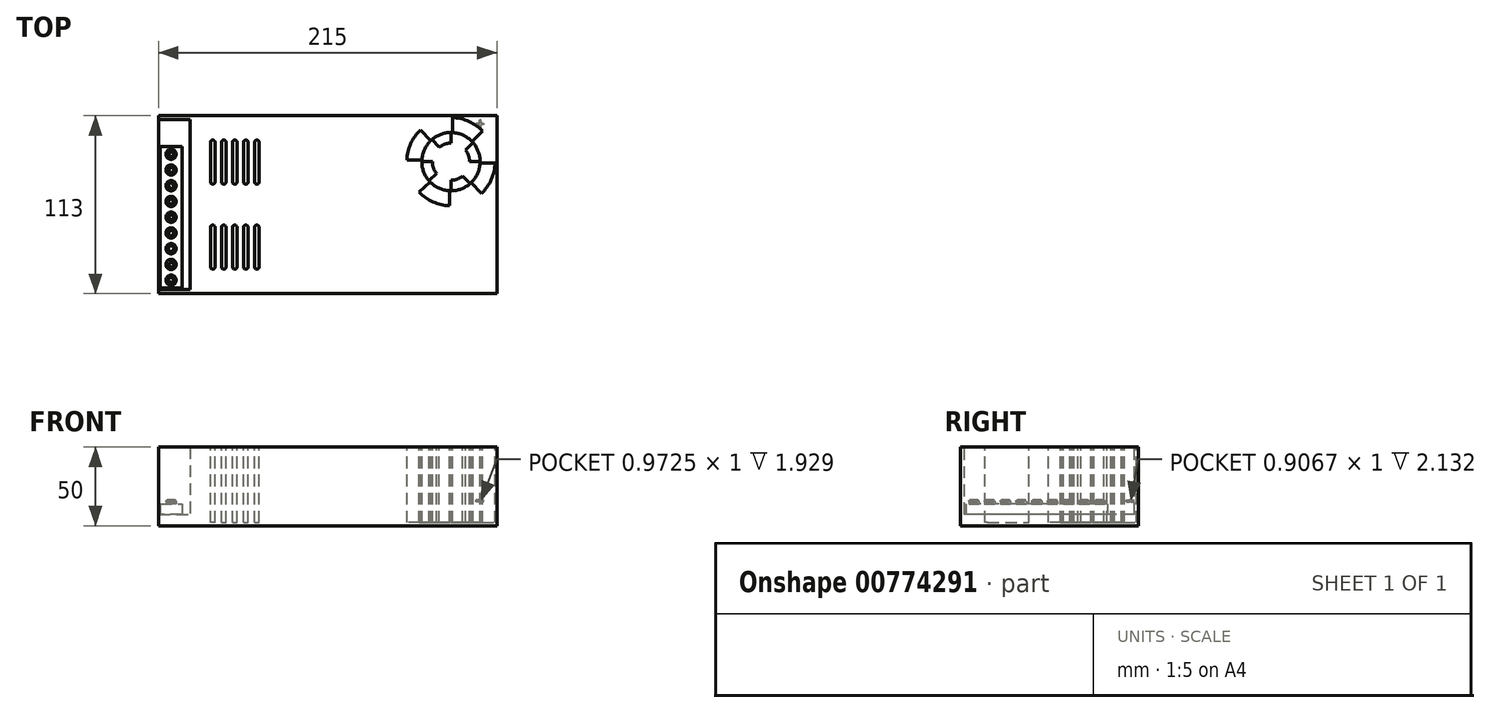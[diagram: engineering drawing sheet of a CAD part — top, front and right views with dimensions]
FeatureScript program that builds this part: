
annotation { "Feature Type Name" : "Feature", "Feature Type Description" : "" }
export const myFeature = defineFeature(function(context is Context, id is Id, definition is map)
    precondition{}
    {
        {
            var Q0;
            Q0=qCreatedBy(makeId("Top.planeOp"),FACE);
            var sketch = newSketch(context, id + "F0", { "sketchPlane" : qUnion([Q0])});
            skLineSegment(sketch, "E0.bottom", {"start": v(-204.25, 5.3) * mm, "end": v(10.75, 5.3) * mm});
            skLineSegment(sketch, "E0.top", {"start": v(-204.25, -107.7) * mm, "end": v(10.75, -107.7) * mm});
            skLineSegment(sketch, "E0.left", {"start": v(-204.25, 5.3) * mm, "end": v(-204.25, -107.7) * mm});
            skLineSegment(sketch, "E0.right", {"start": v(10.75, 5.3) * mm, "end": v(10.75, -107.7) * mm});
            skLineSegment(sketch, "E1", {"start": v(-184.25, 5.3) * mm, "end": v(-184.25, -107.7) * mm});
            skSolve(sketch);
        }
        {
            var Q0;
            {var subQ0=sQuery(id+"F0.wireOp",EDGE,"E0.left");Q0=makeQuery(id+"F0.imprint","IMPRINT",FACE,{"disambiguationData":[TD([[makeQuery(id+"F0.imprint","IMPRINT",EDGE,{"derivedFrom":subQ0}),1.0]])]});}
            extrude(context, id + "F1", {"entities" : qUnion([Q0]), "depth" : .8 * mm, "offsetDistance" : 25 * mm});
        }
        {
            var Q0;
            {var subQ0=sQuery(id+"F0.wireOp",EDGE,"E0.right");Q0=makeQuery(id+"F0.imprint","IMPRINT",FACE,{"disambiguationData":[TD([[makeQuery(id+"F0.imprint","IMPRINT",EDGE,{"derivedFrom":subQ0}),-1.0]])]});}
            extrude(context, id + "F2", {"entities" : qUnion([Q0]), "operationType" : NewBodyOperationType.ADD, "depth" : 50 * mm, "offsetDistance" : 25 * mm});
        }
        {
            var Q0;
            Q0=sQuery(id+"F0.wireOp",EDGE,"E0.bottom");
            extrude(context, id + "F3", {"bodyType" : ToolBodyType.SURFACE, "surfaceEntities" : qUnion([Q0]), "depth" : 50 * mm, "offsetDistance" : 25 * mm});
        }
        {
            var Q0;
            Q0=makeQuery(id+"F3.opExtrude","SWEPT_FACE",FACE,{"disambiguationData":[OSD([sQuery(id+"F0.wireOp",EDGE,"E0.bottom")])]});
            extrude(context, id + "F4", {"entities" : qUnion([Q0]), "operationType" : NewBodyOperationType.ADD, "depth" : 2.5 * mm, "offsetDistance" : 25 * mm});
        }
        {
            var Q0;
            Q0=sQuery(id+"F0.wireOp",EDGE,"E0.top");
            extrude(context, id + "F5", {"bodyType" : ToolBodyType.SURFACE, "surfaceEntities" : qUnion([Q0]), "depth" : 50 * mm, "offsetDistance" : 25 * mm});
        }
        {
            var Q0;
            Q0=makeQuery(id+"F5.opExtrude","SWEPT_FACE",FACE,{"disambiguationData":[OSD([sQuery(id+"F0.wireOp",EDGE,"E0.top")])]});
            extrude(context, id + "F6", {"entities" : qUnion([Q0]), "operationType" : NewBodyOperationType.ADD, "oppositeDirection" : true, "depth" : 2.5 * mm, "offsetDistance" : 25 * mm});
        }
        {
            var Q0;
            Q0=makeQuery(id+"F1.opExtrude","CAP_FACE",FACE,{"disambiguationData":[OSD([sQuery(id+"F0.wireOp",EDGE,"E0.bottom"),sQuery(id+"F0.wireOp",EDGE,"E0.top"),sQuery(id+"F0.wireOp",EDGE,"E0.left"),sQuery(id+"F0.wireOp",EDGE,"E1")])],"isStart":false});
            extrude(context, id + "F7", {"entities" : qUnion([Q0]), "operationType" : NewBodyOperationType.ADD, "depth" : 6.5 * mm, "offsetDistance" : 25 * mm});
        }
        {
            var Q0;
            Q0=makeQuery(id+"F7.opExtrude","CAP_FACE",FACE,{"disambiguationData":[OSD([sQuery(id+"F0.wireOp",EDGE,"E0.bottom"),sQuery(id+"F0.wireOp",EDGE,"E0.top"),sQuery(id+"F0.wireOp",EDGE,"E0.left"),sQuery(id+"F0.wireOp",EDGE,"E1")])],"isStart":false});
            var sketch = newSketch(context, id + "F8", { "sketchPlane" : qUnion([Q0])});
            skLineSegment(sketch, "E2.bottom", {"start": v(-203.25, -14.2) * mm, "end": v(-189.25, -14.2) * mm});
            skLineSegment(sketch, "E2.left", {"start": v(-203.25, -14.2) * mm, "end": v(-203.25, -101.2) * mm});
            skLineSegment(sketch, "E2.right", {"start": v(-189.25, -14.2) * mm, "end": v(-189.25, -104.2) * mm});
            skLineSegment(sketch, "E3", {"start": v(-189.25, -24.2) * mm, "end": v(-203.25, -24.2) * mm});
            skLineSegment(sketch, "E4", {"start": v(-189.25, -34.2) * mm, "end": v(-203.25, -34.2) * mm});
            skLineSegment(sketch, "E5", {"start": v(-189.25, -44.2) * mm, "end": v(-203.25, -44.2) * mm});
            skLineSegment(sketch, "E6", {"start": v(-189.25, -54.2) * mm, "end": v(-203.25, -54.2) * mm});
            skLineSegment(sketch, "E7", {"start": v(-189.25, -64.2) * mm, "end": v(-203.25, -64.2) * mm});
            skLineSegment(sketch, "E8", {"start": v(-189.25, -74.2) * mm, "end": v(-203.25, -74.2) * mm});
            skLineSegment(sketch, "E9", {"start": v(-189.25, -84.2) * mm, "end": v(-203.25, -84.2) * mm});
            skLineSegment(sketch, "E10", {"start": v(-189.25, -94.2) * mm, "end": v(-203.25, -94.2) * mm});
            skLineSegment(sketch, "E11", {"start": v(-189.25, -104.2) * mm, "end": v(-203.25, -104.2) * mm});
            skLineSegment(sketch, "E12", {"start": v(-203.25, -101.2) * mm, "end": v(-203.25, -104.2) * mm});
            skLineSegment(sketch, "E13", {"start": v(-196.25, -14.2) * mm, "end": v(-196.25, -24.2) * mm});
            skCircle(sketch, "E14", {"center": v(-196.25, -19.2) * mm, "radius": 3.25 * mm});
            skLineSegment(sketch, "E15", {"start": v(-189.25, -24.2) * mm, "end": v(-203.25, -34.2) * mm});
            skLineSegment(sketch, "E16", {"start": v(-189.25, -34.2) * mm, "end": v(-203.25, -44.2) * mm});
            skLineSegment(sketch, "E17", {"start": v(-189.25, -44.2) * mm, "end": v(-203.25, -54.2) * mm});
            skLineSegment(sketch, "E18", {"start": v(-189.25, -54.2) * mm, "end": v(-203.25, -64.2) * mm});
            skLineSegment(sketch, "E19", {"start": v(-189.25, -64.2) * mm, "end": v(-203.25, -74.2) * mm});
            skLineSegment(sketch, "E20", {"start": v(-189.25, -74.2) * mm, "end": v(-203.25, -84.2) * mm});
            skLineSegment(sketch, "E21", {"start": v(-189.25, -84.2) * mm, "end": v(-203.25, -94.2) * mm});
            skLineSegment(sketch, "E22", {"start": v(-189.25, -94.2) * mm, "end": v(-203.25, -104.2) * mm});
            skCircle(sketch, "E23", {"center": v(-196.25, -29.2) * mm, "radius": 3.25 * mm});
            skCircle(sketch, "E24", {"center": v(-196.25, -39.2) * mm, "radius": 3.25 * mm});
            skCircle(sketch, "E25", {"center": v(-196.25, -49.2) * mm, "radius": 3.25 * mm});
            skCircle(sketch, "E26", {"center": v(-196.25, -59.2) * mm, "radius": 3.25 * mm});
            skCircle(sketch, "E27", {"center": v(-196.25, -69.2) * mm, "radius": 3.25 * mm});
            skCircle(sketch, "E28", {"center": v(-196.25, -79.2) * mm, "radius": 3.25 * mm});
            skCircle(sketch, "E29", {"center": v(-196.25, -89.2) * mm, "radius": 3.25 * mm});
            skCircle(sketch, "E30", {"center": v(-196.25, -99.2) * mm, "radius": 3.25 * mm});
            skSolve(sketch);
        }
        {
            var Q0;
            Q0 = qSketchRegion(id + "F8", true);
            extrude(context, id + "F9", {"entities" : qUnion([Q0]), "operationType" : NewBodyOperationType.ADD, "depth" : 6.5 * mm, "offsetDistance" : 25 * mm});
        }
        {
            var Q0;
            Q0=makeQuery(id+"F9.boolean.opBoolean","SPLIT",FACE,{"disambiguationData":[TD([makeQuery(id+"F9.opExtrude","SWEPT_FACE",FACE,{"disambiguationData":[OSD([sQuery(id+"F8.wireOp",EDGE,"E14")])]})])],"derivedFrom":makeQuery(id+"F7.opExtrude","CAP_FACE",FACE,{"disambiguationData":[OSD([sQuery(id+"F0.wireOp",EDGE,"E0.bottom"),sQuery(id+"F0.wireOp",EDGE,"E0.top"),sQuery(id+"F0.wireOp",EDGE,"E0.left"),sQuery(id+"F0.wireOp",EDGE,"E1")])],"isStart":false})});
            var Q1;
            Q1=makeQuery(id+"F9.boolean.opBoolean","SPLIT",FACE,{"disambiguationData":[TD([makeQuery(id+"F9.opExtrude","SWEPT_FACE",FACE,{"disambiguationData":[OSD([sQuery(id+"F8.wireOp",EDGE,"E23")])]})])],"derivedFrom":makeQuery(id+"F7.opExtrude","CAP_FACE",FACE,{"disambiguationData":[OSD([sQuery(id+"F0.wireOp",EDGE,"E0.bottom"),sQuery(id+"F0.wireOp",EDGE,"E0.top"),sQuery(id+"F0.wireOp",EDGE,"E0.left"),sQuery(id+"F0.wireOp",EDGE,"E1")])],"isStart":false})});
            var Q2;
            Q2=makeQuery(id+"F9.boolean.opBoolean","SPLIT",FACE,{"disambiguationData":[TD([makeQuery(id+"F9.opExtrude","SWEPT_FACE",FACE,{"disambiguationData":[OSD([sQuery(id+"F8.wireOp",EDGE,"E24")])]})])],"derivedFrom":makeQuery(id+"F7.opExtrude","CAP_FACE",FACE,{"disambiguationData":[OSD([sQuery(id+"F0.wireOp",EDGE,"E0.bottom"),sQuery(id+"F0.wireOp",EDGE,"E0.top"),sQuery(id+"F0.wireOp",EDGE,"E0.left"),sQuery(id+"F0.wireOp",EDGE,"E1")])],"isStart":false})});
            var Q3;
            Q3=makeQuery(id+"F9.boolean.opBoolean","SPLIT",FACE,{"disambiguationData":[TD([makeQuery(id+"F9.opExtrude","SWEPT_FACE",FACE,{"disambiguationData":[OSD([sQuery(id+"F8.wireOp",EDGE,"E25")])]})])],"derivedFrom":makeQuery(id+"F7.opExtrude","CAP_FACE",FACE,{"disambiguationData":[OSD([sQuery(id+"F0.wireOp",EDGE,"E0.bottom"),sQuery(id+"F0.wireOp",EDGE,"E0.top"),sQuery(id+"F0.wireOp",EDGE,"E0.left"),sQuery(id+"F0.wireOp",EDGE,"E1")])],"isStart":false})});
            var Q4;
            Q4=makeQuery(id+"F9.boolean.opBoolean","SPLIT",FACE,{"disambiguationData":[TD([makeQuery(id+"F9.opExtrude","SWEPT_FACE",FACE,{"disambiguationData":[OSD([sQuery(id+"F8.wireOp",EDGE,"E26")])]})])],"derivedFrom":makeQuery(id+"F7.opExtrude","CAP_FACE",FACE,{"disambiguationData":[OSD([sQuery(id+"F0.wireOp",EDGE,"E0.bottom"),sQuery(id+"F0.wireOp",EDGE,"E0.top"),sQuery(id+"F0.wireOp",EDGE,"E0.left"),sQuery(id+"F0.wireOp",EDGE,"E1")])],"isStart":false})});
            var Q5;
            Q5=makeQuery(id+"F9.boolean.opBoolean","SPLIT",FACE,{"disambiguationData":[TD([makeQuery(id+"F9.opExtrude","SWEPT_FACE",FACE,{"disambiguationData":[OSD([sQuery(id+"F8.wireOp",EDGE,"E27")])]})])],"derivedFrom":makeQuery(id+"F7.opExtrude","CAP_FACE",FACE,{"disambiguationData":[OSD([sQuery(id+"F0.wireOp",EDGE,"E0.bottom"),sQuery(id+"F0.wireOp",EDGE,"E0.top"),sQuery(id+"F0.wireOp",EDGE,"E0.left"),sQuery(id+"F0.wireOp",EDGE,"E1")])],"isStart":false})});
            var Q6;
            Q6=makeQuery(id+"F9.boolean.opBoolean","SPLIT",FACE,{"disambiguationData":[TD([makeQuery(id+"F9.opExtrude","SWEPT_FACE",FACE,{"disambiguationData":[OSD([sQuery(id+"F8.wireOp",EDGE,"E28")])]})])],"derivedFrom":makeQuery(id+"F7.opExtrude","CAP_FACE",FACE,{"disambiguationData":[OSD([sQuery(id+"F0.wireOp",EDGE,"E0.bottom"),sQuery(id+"F0.wireOp",EDGE,"E0.top"),sQuery(id+"F0.wireOp",EDGE,"E0.left"),sQuery(id+"F0.wireOp",EDGE,"E1")])],"isStart":false})});
            var Q7;
            Q7=makeQuery(id+"F9.boolean.opBoolean","SPLIT",FACE,{"disambiguationData":[TD([makeQuery(id+"F9.opExtrude","SWEPT_FACE",FACE,{"disambiguationData":[OSD([sQuery(id+"F8.wireOp",EDGE,"E29")])]})])],"derivedFrom":makeQuery(id+"F7.opExtrude","CAP_FACE",FACE,{"disambiguationData":[OSD([sQuery(id+"F0.wireOp",EDGE,"E0.bottom"),sQuery(id+"F0.wireOp",EDGE,"E0.top"),sQuery(id+"F0.wireOp",EDGE,"E0.left"),sQuery(id+"F0.wireOp",EDGE,"E1")])],"isStart":false})});
            var Q8;
            Q8=makeQuery(id+"F9.boolean.opBoolean","SPLIT",FACE,{"disambiguationData":[TD([makeQuery(id+"F9.opExtrude","SWEPT_FACE",FACE,{"disambiguationData":[OSD([sQuery(id+"F8.wireOp",EDGE,"E30")])]})])],"derivedFrom":makeQuery(id+"F7.opExtrude","CAP_FACE",FACE,{"disambiguationData":[OSD([sQuery(id+"F0.wireOp",EDGE,"E0.bottom"),sQuery(id+"F0.wireOp",EDGE,"E0.top"),sQuery(id+"F0.wireOp",EDGE,"E0.left"),sQuery(id+"F0.wireOp",EDGE,"E1")])],"isStart":false})});
            var Q9;
            Q9=sQuery(id+"F8.wireOp",EDGE,"E23");
            var Q10;
            Q10=sQuery(id+"F8.wireOp",EDGE,"E14");
            var Q11;
            Q11=sQuery(id+"F8.wireOp",EDGE,"E24");
            var Q12;
            Q12=sQuery(id+"F8.wireOp",EDGE,"E25");
            var Q13;
            Q13=sQuery(id+"F8.wireOp",EDGE,"E26");
            var Q14;
            Q14=sQuery(id+"F8.wireOp",EDGE,"E27");
            var Q15;
            Q15=sQuery(id+"F8.wireOp",EDGE,"E28");
            var Q16;
            Q16=sQuery(id+"F8.wireOp",EDGE,"E29");
            var Q17;
            Q17=sQuery(id+"F8.wireOp",EDGE,"E30");
            extrude(context, id + "F10", {"entities" : qUnion([Q0, Q1, Q2, Q3, Q4, Q5, Q6, Q7, Q8]), "operationType" : NewBodyOperationType.ADD, "surfaceOperationType" : NewSurfaceOperationType.ADD, "surfaceEntities" : qUnion([Q9, Q10, Q11, Q12, Q13, Q14, Q15, Q16, Q17]), "depth" : 9 * mm, "offsetDistance" : 25 * mm});
        }
        {
            var Q0;
            Q0=makeQuery(id+"F10.opExtrude","CAP_EDGE",EDGE,{"disambiguationData":[OSD([sQuery(id+"F8.wireOp",EDGE,"E14")])],"isStart":false});
            var Q1;
            Q1=makeQuery(id+"F10.opExtrude","CAP_EDGE",EDGE,{"disambiguationData":[OSD([sQuery(id+"F8.wireOp",EDGE,"E23")])],"isStart":false});
            var Q2;
            Q2=makeQuery(id+"F10.opExtrude","CAP_EDGE",EDGE,{"disambiguationData":[OSD([sQuery(id+"F8.wireOp",EDGE,"E24")])],"isStart":false});
            var Q3;
            Q3=makeQuery(id+"F10.opExtrude","CAP_EDGE",EDGE,{"disambiguationData":[OSD([sQuery(id+"F8.wireOp",EDGE,"E25")])],"isStart":false});
            var Q4;
            Q4=makeQuery(id+"F10.opExtrude","CAP_EDGE",EDGE,{"disambiguationData":[OSD([sQuery(id+"F8.wireOp",EDGE,"E26")])],"isStart":false});
            var Q5;
            Q5=makeQuery(id+"F10.opExtrude","CAP_EDGE",EDGE,{"disambiguationData":[OSD([sQuery(id+"F8.wireOp",EDGE,"E27")])],"isStart":false});
            var Q6;
            Q6=makeQuery(id+"F10.opExtrude","CAP_EDGE",EDGE,{"disambiguationData":[OSD([sQuery(id+"F8.wireOp",EDGE,"E28")])],"isStart":false});
            var Q7;
            Q7=makeQuery(id+"F10.opExtrude","CAP_EDGE",EDGE,{"disambiguationData":[OSD([sQuery(id+"F8.wireOp",EDGE,"E29")])],"isStart":false});
            var Q8;
            Q8=makeQuery(id+"F10.opExtrude","CAP_EDGE",EDGE,{"disambiguationData":[OSD([sQuery(id+"F8.wireOp",EDGE,"E30")])],"isStart":false});
            fillet(context, id + "F11", {"entities" : qUnion([Q0, Q1, Q2, Q3, Q4, Q5, Q6, Q7, Q8]), "radius" : .8 * mm, "tangentPropagation" : true, "allowEdgeOverflow" : false});
        }
        {
            var Q0;
            {var subQ0=sQuery(id+"F0.wireOp",EDGE,"E1");var subQ1=sQuery(id+"F0.wireOp",EDGE,"E0.left");var subQ2=sQuery(id+"F0.wireOp",EDGE,"E0.top");var subQ3=sQuery(id+"F0.wireOp",EDGE,"E0.bottom");Q0=makeQuery(id+"F10.opExtrude","CAP_FACE",FACE,{"disambiguationData":[OSD([subQ3,subQ2,subQ1,subQ0]),TDD([makeQuery(id+"F9.boolean.opBoolean","SPLIT",FACE,{"disambiguationData":[TD([makeQuery(id+"F9.opExtrude","SWEPT_FACE",FACE,{"disambiguationData":[OSD([sQuery(id+"F8.wireOp",EDGE,"E14")])]})])],"derivedFrom":makeQuery(id+"F7.opExtrude","CAP_FACE",FACE,{"disambiguationData":[OSD([subQ3,subQ2,subQ1,subQ0])],"isStart":false})})])],"isStart":false});}
            var sketch = newSketch(context, id + "F12", { "sketchPlane" : qUnion([Q0])});
            skLineSegment(sketch, "E31.bottom", {"start": v(-193.85, -18.7) * mm, "end": v(-198.67, -18.7) * mm});
            skLineSegment(sketch, "E31.top", {"start": v(-193.85, -19.6) * mm, "end": v(-198.67, -19.6) * mm});
            skLineSegment(sketch, "E31.left", {"start": v(-193.85, -18.7) * mm, "end": v(-193.85, -19.6) * mm});
            skLineSegment(sketch, "E31.right", {"start": v(-198.67, -18.7) * mm, "end": v(-198.67, -19.6) * mm});
            skLineSegment(sketch, "E32.bottom", {"start": v(-195.56, -21.55) * mm, "end": v(-196.54, -21.55) * mm});
            skLineSegment(sketch, "E32.top", {"start": v(-195.56, -16.77) * mm, "end": v(-196.54, -16.77) * mm});
            skLineSegment(sketch, "E32.left", {"start": v(-195.56, -21.55) * mm, "end": v(-195.56, -16.77) * mm});
            skLineSegment(sketch, "E32.right", {"start": v(-196.54, -21.55) * mm, "end": v(-196.54, -16.77) * mm});
            skSolve(sketch);
        }
        {
            var Q0;
            Q0 = qSketchRegion(id + "F12", true);
            extrude(context, id + "F13", {"entities" : qUnion([Q0]), "operationType" : NewBodyOperationType.REMOVE, "oppositeDirection" : true, "depth" : 1 * mm, "offsetDistance" : 25 * mm});
        }
        {
            var Q0;
            {var subQ0=sQuery(id+"F0.wireOp",EDGE,"E1");var subQ1=sQuery(id+"F0.wireOp",EDGE,"E0.left");var subQ2=sQuery(id+"F0.wireOp",EDGE,"E0.top");var subQ3=sQuery(id+"F0.wireOp",EDGE,"E0.bottom");Q0=makeQuery(id+"F10.opExtrude","CAP_FACE",FACE,{"disambiguationData":[OSD([subQ3,subQ2,subQ1,subQ0]),TDD([makeQuery(id+"F9.boolean.opBoolean","SPLIT",FACE,{"disambiguationData":[TD([makeQuery(id+"F9.opExtrude","SWEPT_FACE",FACE,{"disambiguationData":[OSD([sQuery(id+"F8.wireOp",EDGE,"E23")])]})])],"derivedFrom":makeQuery(id+"F7.opExtrude","CAP_FACE",FACE,{"disambiguationData":[OSD([subQ3,subQ2,subQ1,subQ0])],"isStart":false})})])],"isStart":false});}
            var sketch = newSketch(context, id + "F14", { "sketchPlane" : qUnion([Q0])});
            skLineSegment(sketch, "E33.bottom", {"start": v(2.3, 0.46) * mm, "end": v(-2.51, 0.46) * mm});
            skLineSegment(sketch, "E33.top", {"start": v(2.3, -0.45) * mm, "end": v(-2.51, -0.45) * mm});
            skLineSegment(sketch, "E33.left", {"start": v(2.3, 0.46) * mm, "end": v(2.3, -0.45) * mm});
            skLineSegment(sketch, "E33.right", {"start": v(-2.51, 0.46) * mm, "end": v(-2.51, -0.45) * mm});
            skLineSegment(sketch, "E34.bottom", {"start": v(0.6, -2.4) * mm, "end": v(-0.38, -2.4) * mm});
            skLineSegment(sketch, "E34.top", {"start": v(0.6, 2.39) * mm, "end": v(-0.38, 2.39) * mm});
            skLineSegment(sketch, "E34.left", {"start": v(0.6, -2.4) * mm, "end": v(0.6, 2.39) * mm});
            skLineSegment(sketch, "E34.right", {"start": v(-0.38, -2.4) * mm, "end": v(-0.38, 2.39) * mm});
            skLineSegment(sketch, "E35.bottom", {"start": v(-193.86, -28.65) * mm, "end": v(-198.64, -28.65) * mm});
            skLineSegment(sketch, "E35.top", {"start": v(-193.86, -29.75) * mm, "end": v(-198.64, -29.75) * mm});
            skLineSegment(sketch, "E35.left", {"start": v(-193.86, -28.65) * mm, "end": v(-193.86, -29.75) * mm});
            skLineSegment(sketch, "E35.right", {"start": v(-198.64, -28.65) * mm, "end": v(-198.64, -29.75) * mm});
            skLineSegment(sketch, "E36.bottom", {"start": v(-195.54, -31.55) * mm, "end": v(-196.58, -31.55) * mm});
            skLineSegment(sketch, "E36.top", {"start": v(-195.54, -26.85) * mm, "end": v(-196.58, -26.85) * mm});
            skLineSegment(sketch, "E36.left", {"start": v(-195.54, -31.55) * mm, "end": v(-195.54, -26.85) * mm});
            skLineSegment(sketch, "E36.right", {"start": v(-196.58, -31.55) * mm, "end": v(-196.58, -26.85) * mm});
            skSolve(sketch);
        }
        {
            var Q0;
            Q0 = qSketchRegion(id + "F14", true);
            extrude(context, id + "F15", {"entities" : qUnion([Q0]), "operationType" : NewBodyOperationType.REMOVE, "oppositeDirection" : true, "depth" : 1 * mm, "offsetDistance" : 25 * mm});
        }
        {
            var Q0;
            {var subQ0=sQuery(id+"F0.wireOp",EDGE,"E1");var subQ1=sQuery(id+"F0.wireOp",EDGE,"E0.left");var subQ2=sQuery(id+"F0.wireOp",EDGE,"E0.top");var subQ3=sQuery(id+"F0.wireOp",EDGE,"E0.bottom");Q0=makeQuery(id+"F10.opExtrude","CAP_FACE",FACE,{"disambiguationData":[OSD([subQ3,subQ2,subQ1,subQ0]),TDD([makeQuery(id+"F9.boolean.opBoolean","SPLIT",FACE,{"disambiguationData":[TD([makeQuery(id+"F9.opExtrude","SWEPT_FACE",FACE,{"disambiguationData":[OSD([sQuery(id+"F8.wireOp",EDGE,"E24")])]})])],"derivedFrom":makeQuery(id+"F7.opExtrude","CAP_FACE",FACE,{"disambiguationData":[OSD([subQ3,subQ2,subQ1,subQ0])],"isStart":false})})])],"isStart":false});}
            var sketch = newSketch(context, id + "F16", { "sketchPlane" : qUnion([Q0])});
            skLineSegment(sketch, "E37.bottom", {"start": v(-194.22, -37.83) * mm, "end": v(-198.7, -39.21) * mm});
            skLineSegment(sketch, "E37.top", {"start": v(-193.8, -39.19) * mm, "end": v(-198.28, -40.57) * mm});
            skLineSegment(sketch, "E37.left", {"start": v(-194.22, -37.83) * mm, "end": v(-193.8, -39.19) * mm});
            skLineSegment(sketch, "E37.right", {"start": v(-198.7, -39.21) * mm, "end": v(-198.28, -40.57) * mm});
            skLineSegment(sketch, "E38.bottom", {"start": v(-195.1, -41.36) * mm, "end": v(-195.99, -41.64) * mm});
            skLineSegment(sketch, "E38.top", {"start": v(-196.51, -36.76) * mm, "end": v(-197.4, -37.04) * mm});
            skLineSegment(sketch, "E38.left", {"start": v(-195.1, -41.36) * mm, "end": v(-196.51, -36.76) * mm});
            skLineSegment(sketch, "E38.right", {"start": v(-195.99, -41.64) * mm, "end": v(-197.4, -37.04) * mm});
            skSolve(sketch);
        }
        {
            var Q0;
            Q0 = qSketchRegion(id + "F16", true);
            extrude(context, id + "F17", {"entities" : qUnion([Q0]), "operationType" : NewBodyOperationType.REMOVE, "oppositeDirection" : true, "depth" : 1 * mm, "offsetDistance" : 25 * mm});
        }
        {
            var Q0;
            {var subQ0=sQuery(id+"F0.wireOp",EDGE,"E1");var subQ1=sQuery(id+"F0.wireOp",EDGE,"E0.left");var subQ2=sQuery(id+"F0.wireOp",EDGE,"E0.top");var subQ3=sQuery(id+"F0.wireOp",EDGE,"E0.bottom");Q0=makeQuery(id+"F10.opExtrude","CAP_FACE",FACE,{"disambiguationData":[OSD([subQ3,subQ2,subQ1,subQ0]),TDD([makeQuery(id+"F9.boolean.opBoolean","SPLIT",FACE,{"disambiguationData":[TD([makeQuery(id+"F9.opExtrude","SWEPT_FACE",FACE,{"disambiguationData":[OSD([sQuery(id+"F8.wireOp",EDGE,"E25")])]})])],"derivedFrom":makeQuery(id+"F7.opExtrude","CAP_FACE",FACE,{"disambiguationData":[OSD([subQ3,subQ2,subQ1,subQ0])],"isStart":false})})])],"isStart":false});}
            var sketch = newSketch(context, id + "F18", { "sketchPlane" : qUnion([Q0])});
            skLineSegment(sketch, "E39.bottom", {"start": v(-194.47, -50.88) * mm, "end": v(-198.7, -48.73) * mm});
            skLineSegment(sketch, "E39.top", {"start": v(-193.92, -49.8) * mm, "end": v(-198.15, -47.65) * mm});
            skLineSegment(sketch, "E39.left", {"start": v(-193.92, -49.8) * mm, "end": v(-194.47, -50.88) * mm});
            skLineSegment(sketch, "E39.right", {"start": v(-198.15, -47.65) * mm, "end": v(-198.7, -48.73) * mm});
            skLineSegment(sketch, "E40.bottom", {"start": v(-196.92, -51.57) * mm, "end": v(-197.72, -51.16) * mm});
            skLineSegment(sketch, "E40.top", {"start": v(-194.73, -47.27) * mm, "end": v(-195.53, -46.86) * mm});
            skLineSegment(sketch, "E40.left", {"start": v(-197.72, -51.16) * mm, "end": v(-195.53, -46.86) * mm});
            skLineSegment(sketch, "E40.right", {"start": v(-196.92, -51.57) * mm, "end": v(-194.73, -47.27) * mm});
            skSolve(sketch);
        }
        {
            var Q0;
            {var subQ0=sQuery(id+"F18.wireOp",EDGE,"E40.left");var subQ1=sQuery(id+"F18.wireOp",EDGE,"E39.bottom");var subQ2=makeQuery(id+"F18.imprint","INTERSECT",VERTEX,{"derivedFrom":[subQ1,subQ0]});Q0=makeQuery(id+"F18.imprint","IMPRINT",FACE,{"disambiguationData":[TD([[makeQuery(id+"F18.imprint","IMPRINT",EDGE,{"disambiguationData":[TD([[subQ2,-1.0]])],"derivedFrom":subQ0}),1.0]])]});}
            var Q1;
            {var subQ9=sQuery(id+"F18.wireOp",EDGE,"E39.top");var subQ11=sQuery(id+"F18.wireOp",EDGE,"E40.right");var subQ12=makeQuery(id+"F18.imprint","INTERSECT",VERTEX,{"derivedFrom":[subQ9,subQ11]});Q1=makeQuery(id+"F18.imprint","IMPRINT",FACE,{"disambiguationData":[TD([[makeQuery(id+"F18.imprint","IMPRINT",EDGE,{"disambiguationData":[TD([[subQ12,-1.0]])],"derivedFrom":subQ9}),-1.0]])]});}
            var Q2;
            {var subQ0=sQuery(id+"F18.wireOp",EDGE,"E40.right");var subQ1=sQuery(id+"F18.wireOp",EDGE,"E39.bottom");var subQ2=makeQuery(id+"F18.imprint","INTERSECT",VERTEX,{"derivedFrom":[subQ1,subQ0]});Q2=makeQuery(id+"F18.imprint","IMPRINT",FACE,{"disambiguationData":[TD([[makeQuery(id+"F18.imprint","IMPRINT",EDGE,{"disambiguationData":[TD([[subQ2,-1.0]])],"derivedFrom":subQ1}),-1.0]])]});}
            var Q3;
            {var subQ0=sQuery(id+"F18.wireOp",EDGE,"E39.left");Q3=makeQuery(id+"F18.imprint","IMPRINT",FACE,{"disambiguationData":[TD([[makeQuery(id+"F18.imprint","IMPRINT",EDGE,{"derivedFrom":subQ0}),-1.0]])]});}
            var Q4;
            {var subQ0=sQuery(id+"F18.wireOp",EDGE,"E40.right");var subQ1=sQuery(id+"F18.wireOp",EDGE,"E39.bottom");var subQ2=makeQuery(id+"F18.imprint","INTERSECT",VERTEX,{"derivedFrom":[subQ1,subQ0]});Q4=makeQuery(id+"F18.imprint","IMPRINT",FACE,{"disambiguationData":[TD([[makeQuery(id+"F18.imprint","IMPRINT",EDGE,{"disambiguationData":[TD([[subQ2,-1.0]])],"derivedFrom":subQ1}),1.0]])]});}
            extrude(context, id + "F19", {"entities" : qUnion([Q0, Q1, Q2, Q3, Q4]), "operationType" : NewBodyOperationType.REMOVE, "oppositeDirection" : true, "depth" : 1 * mm, "offsetDistance" : 25 * mm});
        }
        {
            var Q0;
            {var subQ0=sQuery(id+"F0.wireOp",EDGE,"E1");var subQ1=sQuery(id+"F0.wireOp",EDGE,"E0.left");var subQ2=sQuery(id+"F0.wireOp",EDGE,"E0.top");var subQ3=sQuery(id+"F0.wireOp",EDGE,"E0.bottom");Q0=makeQuery(id+"F10.opExtrude","CAP_FACE",FACE,{"disambiguationData":[OSD([subQ3,subQ2,subQ1,subQ0]),TDD([makeQuery(id+"F9.boolean.opBoolean","SPLIT",FACE,{"disambiguationData":[TD([makeQuery(id+"F9.opExtrude","SWEPT_FACE",FACE,{"disambiguationData":[OSD([sQuery(id+"F8.wireOp",EDGE,"E26")])]})])],"derivedFrom":makeQuery(id+"F7.opExtrude","CAP_FACE",FACE,{"disambiguationData":[OSD([subQ3,subQ2,subQ1,subQ0])],"isStart":false})})])],"isStart":false});}
            var sketch = newSketch(context, id + "F20", { "sketchPlane" : qUnion([Q0])});
            skLineSegment(sketch, "E41.bottom", {"start": v(-193.82, -58.7) * mm, "end": v(-198.63, -58.7) * mm});
            skLineSegment(sketch, "E41.top", {"start": v(-193.82, -59.6) * mm, "end": v(-198.63, -59.6) * mm});
            skLineSegment(sketch, "E41.left", {"start": v(-193.82, -58.7) * mm, "end": v(-193.82, -59.6) * mm});
            skLineSegment(sketch, "E41.right", {"start": v(-198.63, -58.7) * mm, "end": v(-198.63, -59.6) * mm});
            skLineSegment(sketch, "E42.bottom", {"start": v(-195.53, -61.56) * mm, "end": v(-196.5, -61.56) * mm});
            skLineSegment(sketch, "E42.top", {"start": v(-195.53, -56.77) * mm, "end": v(-196.5, -56.77) * mm});
            skLineSegment(sketch, "E42.left", {"start": v(-195.53, -61.56) * mm, "end": v(-195.53, -56.77) * mm});
            skLineSegment(sketch, "E42.right", {"start": v(-196.5, -61.56) * mm, "end": v(-196.5, -56.77) * mm});
            skSolve(sketch);
        }
        {
            var Q0;
            Q0 = qSketchRegion(id + "F20", true);
            extrude(context, id + "F21", {"entities" : qUnion([Q0]), "operationType" : NewBodyOperationType.REMOVE, "oppositeDirection" : true, "depth" : 1 * mm, "offsetDistance" : 25 * mm});
        }
        {
            var Q0;
            {var subQ0=sQuery(id+"F0.wireOp",EDGE,"E1");var subQ1=sQuery(id+"F0.wireOp",EDGE,"E0.left");var subQ2=sQuery(id+"F0.wireOp",EDGE,"E0.top");var subQ3=sQuery(id+"F0.wireOp",EDGE,"E0.bottom");Q0=makeQuery(id+"F10.opExtrude","CAP_FACE",FACE,{"disambiguationData":[OSD([subQ3,subQ2,subQ1,subQ0]),TDD([makeQuery(id+"F9.boolean.opBoolean","SPLIT",FACE,{"disambiguationData":[TD([makeQuery(id+"F9.opExtrude","SWEPT_FACE",FACE,{"disambiguationData":[OSD([sQuery(id+"F8.wireOp",EDGE,"E27")])]})])],"derivedFrom":makeQuery(id+"F7.opExtrude","CAP_FACE",FACE,{"disambiguationData":[OSD([subQ3,subQ2,subQ1,subQ0])],"isStart":false})})])],"isStart":false});}
            var sketch = newSketch(context, id + "F22", { "sketchPlane" : qUnion([Q0])});
            skLineSegment(sketch, "E43.bottom", {"start": v(-193.9, -69.86) * mm, "end": v(-197.88, -67.37) * mm});
            skLineSegment(sketch, "E43.top", {"start": v(-194.62, -71.03) * mm, "end": v(-198.6, -68.54) * mm});
            skLineSegment(sketch, "E43.left", {"start": v(-193.9, -69.86) * mm, "end": v(-194.62, -71.03) * mm});
            skLineSegment(sketch, "E43.right", {"start": v(-197.88, -67.37) * mm, "end": v(-198.6, -68.54) * mm});
            skLineSegment(sketch, "E44.bottom", {"start": v(-197, -71.6) * mm, "end": v(-197.82, -71.08) * mm});
            skLineSegment(sketch, "E44.top", {"start": v(-194.43, -67.48) * mm, "end": v(-195.25, -66.96) * mm});
            skLineSegment(sketch, "E44.left", {"start": v(-197, -71.6) * mm, "end": v(-194.43, -67.48) * mm});
            skLineSegment(sketch, "E44.right", {"start": v(-197.82, -71.08) * mm, "end": v(-195.25, -66.96) * mm});
            skSolve(sketch);
        }
        {
            var Q0;
            Q0 = qSketchRegion(id + "F22", true);
            extrude(context, id + "F23", {"entities" : qUnion([Q0]), "operationType" : NewBodyOperationType.REMOVE, "oppositeDirection" : true, "depth" : 1 * mm, "offsetDistance" : 25 * mm});
        }
        {
            var Q0;
            {var subQ0=sQuery(id+"F0.wireOp",EDGE,"E1");var subQ1=sQuery(id+"F0.wireOp",EDGE,"E0.left");var subQ2=sQuery(id+"F0.wireOp",EDGE,"E0.top");var subQ3=sQuery(id+"F0.wireOp",EDGE,"E0.bottom");Q0=makeQuery(id+"F10.opExtrude","CAP_FACE",FACE,{"disambiguationData":[OSD([subQ3,subQ2,subQ1,subQ0]),TDD([makeQuery(id+"F9.boolean.opBoolean","SPLIT",FACE,{"disambiguationData":[TD([makeQuery(id+"F9.opExtrude","SWEPT_FACE",FACE,{"disambiguationData":[OSD([sQuery(id+"F8.wireOp",EDGE,"E28")])]})])],"derivedFrom":makeQuery(id+"F7.opExtrude","CAP_FACE",FACE,{"disambiguationData":[OSD([subQ3,subQ2,subQ1,subQ0])],"isStart":false})})])],"isStart":false});}
            var sketch = newSketch(context, id + "F24", { "sketchPlane" : qUnion([Q0])});
            skLineSegment(sketch, "E45.bottom", {"start": v(-193.8, -79.39) * mm, "end": v(-198.17, -77.67) * mm});
            skLineSegment(sketch, "E45.top", {"start": v(-194.33, -80.73) * mm, "end": v(-198.7, -79.01) * mm});
            skLineSegment(sketch, "E45.left", {"start": v(-193.8, -79.39) * mm, "end": v(-194.33, -80.73) * mm});
            skLineSegment(sketch, "E45.right", {"start": v(-198.17, -77.67) * mm, "end": v(-198.7, -79.01) * mm});
            skLineSegment(sketch, "E46.bottom", {"start": v(-196.37, -81.65) * mm, "end": v(-197.83, -81.07) * mm});
            skLineSegment(sketch, "E46.top", {"start": v(-194.67, -77.33) * mm, "end": v(-196.13, -76.75) * mm});
            skLineSegment(sketch, "E46.left", {"start": v(-196.37, -81.65) * mm, "end": v(-194.67, -77.33) * mm});
            skLineSegment(sketch, "E46.right", {"start": v(-197.83, -81.07) * mm, "end": v(-196.13, -76.75) * mm});
            skSolve(sketch);
        }
        {
            var Q0;
            Q0 = qSketchRegion(id + "F24", true);
            extrude(context, id + "F25", {"entities" : qUnion([Q0]), "operationType" : NewBodyOperationType.REMOVE, "oppositeDirection" : true, "depth" : 1 * mm, "offsetDistance" : 25 * mm});
        }
        {
            var Q0;
            {var subQ0=sQuery(id+"F0.wireOp",EDGE,"E1");var subQ1=sQuery(id+"F0.wireOp",EDGE,"E0.left");var subQ2=sQuery(id+"F0.wireOp",EDGE,"E0.top");var subQ3=sQuery(id+"F0.wireOp",EDGE,"E0.bottom");Q0=makeQuery(id+"F10.opExtrude","CAP_FACE",FACE,{"disambiguationData":[OSD([subQ3,subQ2,subQ1,subQ0]),TDD([makeQuery(id+"F9.boolean.opBoolean","SPLIT",FACE,{"disambiguationData":[TD([makeQuery(id+"F9.opExtrude","SWEPT_FACE",FACE,{"disambiguationData":[OSD([sQuery(id+"F8.wireOp",EDGE,"E29")])]})])],"derivedFrom":makeQuery(id+"F7.opExtrude","CAP_FACE",FACE,{"disambiguationData":[OSD([subQ3,subQ2,subQ1,subQ0])],"isStart":false})})])],"isStart":false});}
            var sketch = newSketch(context, id + "F26", { "sketchPlane" : qUnion([Q0])});
            skLineSegment(sketch, "E47.bottom", {"start": v(-193.9, -88.84) * mm, "end": v(-198.7, -88.84) * mm});
            skLineSegment(sketch, "E47.top", {"start": v(-193.9, -89.75) * mm, "end": v(-198.7, -89.75) * mm});
            skLineSegment(sketch, "E47.left", {"start": v(-193.9, -88.84) * mm, "end": v(-193.9, -89.75) * mm});
            skLineSegment(sketch, "E47.right", {"start": v(-198.7, -88.84) * mm, "end": v(-198.7, -89.75) * mm});
            skLineSegment(sketch, "E48.bottom", {"start": v(-195.61, -91.57) * mm, "end": v(-196.65, -91.57) * mm});
            skLineSegment(sketch, "E48.top", {"start": v(-195.61, -86.78) * mm, "end": v(-196.65, -86.78) * mm});
            skLineSegment(sketch, "E48.left", {"start": v(-195.61, -91.57) * mm, "end": v(-195.61, -86.78) * mm});
            skLineSegment(sketch, "E48.right", {"start": v(-196.65, -91.57) * mm, "end": v(-196.65, -86.78) * mm});
            skSolve(sketch);
        }
        {
            var Q0;
            {var subQ0=sQuery(id+"F26.wireOp",EDGE,"E48.left");var subQ1=sQuery(id+"F26.wireOp",EDGE,"E47.bottom");var subQ2=makeQuery(id+"F26.imprint","INTERSECT",VERTEX,{"derivedFrom":[subQ1,subQ0]});Q0=makeQuery(id+"F26.imprint","IMPRINT",FACE,{"disambiguationData":[TD([[makeQuery(id+"F26.imprint","IMPRINT",EDGE,{"disambiguationData":[TD([[subQ2,-1.0]])],"derivedFrom":subQ1}),1.0]])]});}
            var Q1;
            {var subQ9=sQuery(id+"F26.wireOp",EDGE,"E47.bottom");var subQ11=sQuery(id+"F26.wireOp",EDGE,"E48.left");var subQ12=makeQuery(id+"F26.imprint","INTERSECT",VERTEX,{"derivedFrom":[subQ9,subQ11]});Q1=makeQuery(id+"F26.imprint","IMPRINT",FACE,{"disambiguationData":[TD([[makeQuery(id+"F26.imprint","IMPRINT",EDGE,{"disambiguationData":[TD([[subQ12,-1.0]])],"derivedFrom":subQ9}),-1.0]])]});}
            var Q2;
            {var subQ0=sQuery(id+"F26.wireOp",EDGE,"E48.right");var subQ1=sQuery(id+"F26.wireOp",EDGE,"E47.bottom");var subQ2=makeQuery(id+"F26.imprint","INTERSECT",VERTEX,{"derivedFrom":[subQ1,subQ0]});Q2=makeQuery(id+"F26.imprint","IMPRINT",FACE,{"disambiguationData":[TD([[makeQuery(id+"F26.imprint","IMPRINT",EDGE,{"disambiguationData":[TD([[subQ2,1.0]])],"derivedFrom":subQ0}),1.0]])]});}
            var Q3;
            {var subQ0=sQuery(id+"F26.wireOp",EDGE,"E47.left");Q3=makeQuery(id+"F26.imprint","IMPRINT",FACE,{"disambiguationData":[TD([[makeQuery(id+"F26.imprint","IMPRINT",EDGE,{"derivedFrom":subQ0}),-1.0]])]});}
            var Q4;
            {var subQ5=sQuery(id+"F26.wireOp",EDGE,"E48.bottom");Q4=makeQuery(id+"F26.imprint","IMPRINT",FACE,{"disambiguationData":[TD([[makeQuery(id+"F26.imprint","IMPRINT",EDGE,{"derivedFrom":subQ5}),-1.0]])]});}
            extrude(context, id + "F27", {"entities" : qUnion([Q0, Q1, Q2, Q3, Q4]), "operationType" : NewBodyOperationType.REMOVE, "oppositeDirection" : true, "depth" : 1 * mm, "offsetDistance" : 25 * mm});
        }
        {
            var Q0;
            {var subQ0=sQuery(id+"F0.wireOp",EDGE,"E1");var subQ1=sQuery(id+"F0.wireOp",EDGE,"E0.left");var subQ2=sQuery(id+"F0.wireOp",EDGE,"E0.top");var subQ3=sQuery(id+"F0.wireOp",EDGE,"E0.bottom");Q0=makeQuery(id+"F10.opExtrude","CAP_FACE",FACE,{"disambiguationData":[OSD([subQ3,subQ2,subQ1,subQ0]),TDD([makeQuery(id+"F9.boolean.opBoolean","SPLIT",FACE,{"disambiguationData":[TD([makeQuery(id+"F9.opExtrude","SWEPT_FACE",FACE,{"disambiguationData":[OSD([sQuery(id+"F8.wireOp",EDGE,"E30")])]})])],"derivedFrom":makeQuery(id+"F7.opExtrude","CAP_FACE",FACE,{"disambiguationData":[OSD([subQ3,subQ2,subQ1,subQ0])],"isStart":false})})])],"isStart":false});}
            var sketch = newSketch(context, id + "F28", { "sketchPlane" : qUnion([Q0])});
            skLineSegment(sketch, "E49.bottom", {"start": v(-193.77, -99.07) * mm, "end": v(-198.45, -98.11) * mm});
            skLineSegment(sketch, "E49.top", {"start": v(-193.98, -100.13) * mm, "end": v(-198.66, -99.17) * mm});
            skLineSegment(sketch, "E49.left", {"start": v(-193.77, -99.07) * mm, "end": v(-193.98, -100.13) * mm});
            skLineSegment(sketch, "E49.right", {"start": v(-198.45, -98.11) * mm, "end": v(-198.66, -99.17) * mm});
            skLineSegment(sketch, "E50.bottom", {"start": v(-196.03, -101.64) * mm, "end": v(-197.4, -101.36) * mm});
            skLineSegment(sketch, "E50.top", {"start": v(-195.1, -97.04) * mm, "end": v(-196.47, -96.76) * mm});
            skLineSegment(sketch, "E50.left", {"start": v(-196.03, -101.64) * mm, "end": v(-195.1, -97.04) * mm});
            skLineSegment(sketch, "E50.right", {"start": v(-197.4, -101.36) * mm, "end": v(-196.47, -96.76) * mm});
            skSolve(sketch);
        }
        {
            var Q0;
            Q0 = qSketchRegion(id + "F28", true);
            extrude(context, id + "F29", {"entities" : qUnion([Q0]), "operationType" : NewBodyOperationType.REMOVE, "oppositeDirection" : true, "depth" : 1 * mm, "offsetDistance" : 25 * mm});
        }
        {
            var Q0;
            {var subQ0=sQuery(id+"F0.wireOp",EDGE,"E0.top");var subQ1=sQuery(id+"F0.wireOp",EDGE,"E0.bottom");Q0=makeQuery(id+"F6.boolean.opBoolean","MERGE",FACE,{"derivedFrom":[makeQuery(id+"F4.boolean.opBoolean","MERGE",FACE,{"derivedFrom":[makeQuery(id+"F2.opExtrude","CAP_FACE",FACE,{"disambiguationData":[OSD([subQ1,subQ0,sQuery(id+"F0.wireOp",EDGE,"E0.right"),sQuery(id+"F0.wireOp",EDGE,"E1")])],"isStart":false}),makeQuery(id+"F4.opExtrude","SWEPT_FACE",FACE,{"disambiguationData":[OSD([subQ1]),TDD([makeQuery(id+"F3.opExtrude","CAP_EDGE",EDGE,{"disambiguationData":[OSD([subQ1])],"isStart":false})])]})]}),makeQuery(id+"F6.opExtrude","SWEPT_FACE",FACE,{"disambiguationData":[OSD([subQ0]),TDD([makeQuery(id+"F5.opExtrude","CAP_EDGE",EDGE,{"disambiguationData":[OSD([subQ0])],"isStart":false})])]})]});}
            var sketch = newSketch(context, id + "F30", { "sketchPlane" : qUnion([Q0])});
            skLineSegment(sketch, "E51", {"start": v(-184.25, -51.2) * mm, "end": v(10.75, -51.2) * mm});
            skLineSegment(sketch, "E52.left", {"start": v(-171.25, -11.7) * mm, "end": v(-171.25, -36.7) * mm});
            skLineSegment(sketch, "E52.right", {"start": v(-140.25, -11.7) * mm, "end": v(-140.25, -36.7) * mm});
            skLineSegment(sketch, "E53", {"start": v(-168.25, -11.7) * mm, "end": v(-168.25, -36.7) * mm});
            skLineSegment(sketch, "E54", {"start": v(-164.25, -11.7) * mm, "end": v(-164.25, -36.7) * mm});
            skLineSegment(sketch, "E55", {"start": v(-161.25, -11.7) * mm, "end": v(-161.25, -36.7) * mm});
            skLineSegment(sketch, "E56", {"start": v(-157.25, -11.7) * mm, "end": v(-157.25, -36.7) * mm});
            skLineSegment(sketch, "E57", {"start": v(-154.25, -11.7) * mm, "end": v(-154.25, -36.7) * mm});
            skLineSegment(sketch, "E58", {"start": v(-150.25, -11.7) * mm, "end": v(-150.25, -36.7) * mm});
            skLineSegment(sketch, "E59", {"start": v(-147.25, -11.7) * mm, "end": v(-147.25, -36.7) * mm});
            skLineSegment(sketch, "E60", {"start": v(-143.25, -11.7) * mm, "end": v(-143.25, -36.7) * mm});
            skArc(sketch, "E61", {"start": v(-168.25, -11.7) * mm, "mid": v(-169.75, -10.2) * mm, "end": v(-171.25, -11.7) * mm});
            skArc(sketch, "E62", {"start": v(-161.25, -11.7) * mm, "mid": v(-162.75, -10.2) * mm, "end": v(-164.25, -11.7) * mm});
            skArc(sketch, "E63", {"start": v(-154.25, -11.7) * mm, "mid": v(-155.75, -10.2) * mm, "end": v(-157.25, -11.7) * mm});
            skArc(sketch, "E64", {"start": v(-147.25, -11.7) * mm, "mid": v(-148.75, -10.2) * mm, "end": v(-150.25, -11.7) * mm});
            skArc(sketch, "E65", {"start": v(-140.25, -11.7) * mm, "mid": v(-141.75, -10.2) * mm, "end": v(-143.25, -11.7) * mm});
            skArc(sketch, "E66.MirrorCS", {"start": v(-168.25, -36.7) * mm, "mid": v(-169.75, -38.2) * mm, "end": v(-171.25, -36.7) * mm});
            skArc(sketch, "E67.MirrorCS", {"start": v(-161.25, -36.7) * mm, "mid": v(-162.75, -38.2) * mm, "end": v(-164.25, -36.7) * mm});
            skArc(sketch, "E68.MirrorCS", {"start": v(-154.25, -36.7) * mm, "mid": v(-155.75, -38.2) * mm, "end": v(-157.25, -36.7) * mm});
            skArc(sketch, "E69.MirrorCS", {"start": v(-147.25, -36.7) * mm, "mid": v(-148.75, -38.2) * mm, "end": v(-150.25, -36.7) * mm});
            skArc(sketch, "E70.MirrorCS", {"start": v(-140.25, -36.7) * mm, "mid": v(-141.75, -38.2) * mm, "end": v(-143.25, -36.7) * mm});
            skArc(sketch, "E71.MirrorCS", {"start": v(-147.25, -65.7) * mm, "mid": v(-148.75, -64.2) * mm, "end": v(-150.25, -65.7) * mm});
            skArc(sketch, "E72.MirrorCS", {"start": v(-154.25, -90.7) * mm, "mid": v(-155.75, -92.2) * mm, "end": v(-157.25, -90.7) * mm});
            skArc(sketch, "E73.MirrorCS", {"start": v(-140.25, -65.7) * mm, "mid": v(-141.75, -64.2) * mm, "end": v(-143.25, -65.7) * mm});
            skArc(sketch, "E74.MirrorCS", {"start": v(-140.25, -90.7) * mm, "mid": v(-141.75, -92.2) * mm, "end": v(-143.25, -90.7) * mm});
            skArc(sketch, "E75.MirrorCS", {"start": v(-154.25, -65.7) * mm, "mid": v(-155.75, -64.2) * mm, "end": v(-157.25, -65.7) * mm});
            skArc(sketch, "E76.MirrorCS", {"start": v(-168.25, -65.7) * mm, "mid": v(-169.75, -64.2) * mm, "end": v(-171.25, -65.7) * mm});
            skArc(sketch, "E77.MirrorCS", {"start": v(-161.25, -65.7) * mm, "mid": v(-162.75, -64.2) * mm, "end": v(-164.25, -65.7) * mm});
            skArc(sketch, "E78.MirrorCS", {"start": v(-147.25, -90.7) * mm, "mid": v(-148.75, -92.2) * mm, "end": v(-150.25, -90.7) * mm});
            skArc(sketch, "E79.MirrorCS", {"start": v(-168.25, -90.7) * mm, "mid": v(-169.75, -92.2) * mm, "end": v(-171.25, -90.7) * mm});
            skArc(sketch, "E80.MirrorCS", {"start": v(-161.25, -90.7) * mm, "mid": v(-162.75, -92.2) * mm, "end": v(-164.25, -90.7) * mm});
            skLineSegment(sketch, "E81.MirrorCS", {"start": v(-147.25, -90.7) * mm, "end": v(-147.25, -65.7) * mm});
            skLineSegment(sketch, "E82.MirrorCS", {"start": v(-150.25, -90.7) * mm, "end": v(-150.25, -65.7) * mm});
            skLineSegment(sketch, "E83.MirrorCS", {"start": v(-157.25, -90.7) * mm, "end": v(-157.25, -65.7) * mm});
            skLineSegment(sketch, "E84.MirrorCS", {"start": v(-143.25, -90.7) * mm, "end": v(-143.25, -65.7) * mm});
            skLineSegment(sketch, "E85.MirrorCS", {"start": v(-164.25, -90.7) * mm, "end": v(-164.25, -65.7) * mm});
            skLineSegment(sketch, "E86.MirrorCS", {"start": v(-168.25, -90.7) * mm, "end": v(-168.25, -65.7) * mm});
            skLineSegment(sketch, "E87.MirrorCS", {"start": v(-171.25, -90.7) * mm, "end": v(-171.25, -65.7) * mm});
            skLineSegment(sketch, "E88.MirrorCS", {"start": v(-161.25, -90.7) * mm, "end": v(-161.25, -65.7) * mm});
            skLineSegment(sketch, "E89.MirrorCS", {"start": v(-140.25, -90.7) * mm, "end": v(-140.25, -65.7) * mm});
            skLineSegment(sketch, "E90.MirrorCS", {"start": v(-154.25, -90.7) * mm, "end": v(-154.25, -65.7) * mm});
            skSolve(sketch);
        }
        {
            var Q0;
            Q0 = qSketchRegion(id + "F30", true);
            extrude(context, id + "F31", {"entities" : qUnion([Q0]), "operationType" : NewBodyOperationType.REMOVE, "oppositeDirection" : true, "depth" : 48 * mm, "offsetDistance" : 25 * mm});
        }
        {
            var Q0;
            {var subQ0=sQuery(id+"F0.wireOp",EDGE,"E0.top");var subQ1=sQuery(id+"F0.wireOp",EDGE,"E0.bottom");Q0=makeQuery(id+"F6.boolean.opBoolean","MERGE",FACE,{"derivedFrom":[makeQuery(id+"F4.boolean.opBoolean","MERGE",FACE,{"derivedFrom":[makeQuery(id+"F2.opExtrude","CAP_FACE",FACE,{"disambiguationData":[OSD([subQ1,subQ0,sQuery(id+"F0.wireOp",EDGE,"E0.right"),sQuery(id+"F0.wireOp",EDGE,"E1")])],"isStart":false}),makeQuery(id+"F4.opExtrude","SWEPT_FACE",FACE,{"disambiguationData":[OSD([subQ1]),TDD([makeQuery(id+"F3.opExtrude","CAP_EDGE",EDGE,{"disambiguationData":[OSD([subQ1])],"isStart":false})])]})]}),makeQuery(id+"F6.opExtrude","SWEPT_FACE",FACE,{"disambiguationData":[OSD([subQ0]),TDD([makeQuery(id+"F5.opExtrude","CAP_EDGE",EDGE,{"disambiguationData":[OSD([subQ0])],"isStart":false})])]})]});}
            var sketch = newSketch(context, id + "F32", { "sketchPlane" : qUnion([Q0])});
            skCircle(sketch, "E91", {"center": v(-18.45, -23.9) * mm, "radius": 28 * mm});
            skCircle(sketch, "E92", {"center": v(-18.45, -23.9) * mm, "radius": 18.5 * mm});
            skLineSegment(sketch, "E93", {"start": v(-18.45, -23.9) * mm, "end": v(9.55, -23.9) * mm});
            skLineSegment(sketch, "E94", {"start": v(-18.45, -23.9) * mm, "end": v(-46.45, -23.9) * mm});
            skLineSegment(sketch, "E95", {"start": v(-18.45, -23.9) * mm, "end": v(-18.45, 4.1) * mm});
            skLineSegment(sketch, "E96", {"start": v(-18.45, -23.9) * mm, "end": v(-18.45, -51.9) * mm});
            skLineSegment(sketch, "E97", {"start": v(-18.45, -23.9) * mm, "end": v(1.72, -4.48) * mm});
            skLineSegment(sketch, "E98", {"start": v(-18.45, -23.9) * mm, "end": v(-37.87, -3.73) * mm});
            skLineSegment(sketch, "E99", {"start": v(-18.45, -23.9) * mm, "end": v(-38.62, -43.32) * mm});
            skLineSegment(sketch, "E100", {"start": v(-18.45, -23.9) * mm, "end": v(0.97, -44.07) * mm});
            skCircle(sketch, "E101", {"center": v(-18.45, -23.9) * mm, "radius": 11.8 * mm});
            skLineSegment(sketch, "E102.0", {"start": v(-19.17, -24.6) * mm, "end": v(0.25, -44.76) * mm});
            skLineSegment(sketch, "E103.0", {"start": v(-17.75, -24.62) * mm, "end": v(2.42, -5.2) * mm});
            skLineSegment(sketch, "E104.0", {"start": v(-17.45, -23.9) * mm, "end": v(-17.45, 4.1) * mm});
            skLineSegment(sketch, "E105.0", {"start": v(-17.73, -23.2) * mm, "end": v(-37.15, -3.03) * mm});
            skLineSegment(sketch, "E106.0", {"start": v(-18.45, -22.9) * mm, "end": v(-46.45, -22.9) * mm});
            skLineSegment(sketch, "E107.0", {"start": v(-19.14, -23.18) * mm, "end": v(-39.31, -42.6) * mm});
            skLineSegment(sketch, "E108.0", {"start": v(-19.45, -23.9) * mm, "end": v(-19.45, -51.9) * mm});
            skLineSegment(sketch, "E109.0", {"start": v(-18.45, -24.9) * mm, "end": v(9.55, -24.9) * mm});
            skSolve(sketch);
        }
        {
            var Q0;
            {var subQ0=sQuery(id+"F32.wireOp",EDGE,"E94");var subQ1=sQuery(id+"F32.wireOp",EDGE,"E92");var subQ2=makeQuery(id+"F32.imprint","INTERSECT",VERTEX,{"derivedFrom":[subQ1,subQ0]});Q0=makeQuery(id+"F32.imprint","IMPRINT",FACE,{"disambiguationData":[TD([[makeQuery(id+"F32.imprint","IMPRINT",EDGE,{"disambiguationData":[TD([[subQ2,-1.0]])],"derivedFrom":subQ1}),1.0]])]});}
            var Q1;
            {var subQ0=sQuery(id+"F32.wireOp",EDGE,"E96");var subQ1=sQuery(id+"F32.wireOp",EDGE,"E92");var subQ2=makeQuery(id+"F32.imprint","INTERSECT",VERTEX,{"derivedFrom":[subQ1,subQ0]});Q1=makeQuery(id+"F32.imprint","IMPRINT",FACE,{"disambiguationData":[TD([[makeQuery(id+"F32.imprint","IMPRINT",EDGE,{"disambiguationData":[TD([[subQ2,-1.0]])],"derivedFrom":subQ1}),1.0]])]});}
            var Q2;
            {var subQ0=sQuery(id+"F32.wireOp",EDGE,"E103.0");var subQ1=sQuery(id+"F32.wireOp",EDGE,"E92");var subQ2=makeQuery(id+"F32.imprint","INTERSECT",VERTEX,{"derivedFrom":[subQ1,subQ0]});Q2=makeQuery(id+"F32.imprint","IMPRINT",FACE,{"disambiguationData":[TD([[makeQuery(id+"F32.imprint","IMPRINT",EDGE,{"disambiguationData":[TD([[subQ2,1.0]])],"derivedFrom":subQ1}),1.0]])]});}
            var Q3;
            {var subQ0=sQuery(id+"F32.wireOp",EDGE,"E95");var subQ1=sQuery(id+"F32.wireOp",EDGE,"E92");var subQ2=makeQuery(id+"F32.imprint","INTERSECT",VERTEX,{"derivedFrom":[subQ1,subQ0]});Q3=makeQuery(id+"F32.imprint","IMPRINT",FACE,{"disambiguationData":[TD([[makeQuery(id+"F32.imprint","IMPRINT",EDGE,{"disambiguationData":[TD([[subQ2,-1.0]])],"derivedFrom":subQ1}),1.0]])]});}
            var Q4;
            {var subQ0=sQuery(id+"F32.wireOp",EDGE,"E98");var subQ1=sQuery(id+"F32.wireOp",EDGE,"E91");var subQ2=makeQuery(id+"F32.imprint","INTERSECT",VERTEX,{"derivedFrom":[subQ1,subQ0]});Q4=makeQuery(id+"F32.imprint","IMPRINT",FACE,{"disambiguationData":[TD([[makeQuery(id+"F32.imprint","IMPRINT",EDGE,{"disambiguationData":[TD([[subQ2,-1.0]])],"derivedFrom":subQ1}),1.0]])]});}
            var Q5;
            {var subQ0=sQuery(id+"F32.wireOp",EDGE,"E97");var subQ1=sQuery(id+"F32.wireOp",EDGE,"E91");var subQ2=makeQuery(id+"F32.imprint","INTERSECT",VERTEX,{"derivedFrom":[subQ1,subQ0]});Q5=makeQuery(id+"F32.imprint","IMPRINT",FACE,{"disambiguationData":[TD([[makeQuery(id+"F32.imprint","IMPRINT",EDGE,{"disambiguationData":[TD([[subQ2,-1.0]])],"derivedFrom":subQ1}),1.0]])]});}
            var Q6;
            {var subQ0=sQuery(id+"F32.wireOp",EDGE,"E100");var subQ1=sQuery(id+"F32.wireOp",EDGE,"E91");var subQ2=makeQuery(id+"F32.imprint","INTERSECT",VERTEX,{"derivedFrom":[subQ1,subQ0]});Q6=makeQuery(id+"F32.imprint","IMPRINT",FACE,{"disambiguationData":[TD([[makeQuery(id+"F32.imprint","IMPRINT",EDGE,{"disambiguationData":[TD([[subQ2,-1.0]])],"derivedFrom":subQ1}),1.0]])]});}
            var Q7;
            {var subQ0=sQuery(id+"F32.wireOp",EDGE,"E99");var subQ1=sQuery(id+"F32.wireOp",EDGE,"E91");var subQ2=makeQuery(id+"F32.imprint","INTERSECT",VERTEX,{"derivedFrom":[subQ1,subQ0]});Q7=makeQuery(id+"F32.imprint","IMPRINT",FACE,{"disambiguationData":[TD([[makeQuery(id+"F32.imprint","IMPRINT",EDGE,{"disambiguationData":[TD([[subQ2,-1.0]])],"derivedFrom":subQ1}),1.0]])]});}
            extrude(context, id + "F33", {"entities" : qUnion([Q0, Q1, Q2, Q3, Q4, Q5, Q6, Q7]), "operationType" : NewBodyOperationType.REMOVE, "oppositeDirection" : true, "depth" : 48 * mm, "offsetDistance" : 25 * mm});
        }
        {
            var Q0;
            Q0=makeQuery(id+"F5.opExtrude","SWEPT_FACE",FACE,{"disambiguationData":[OSD([sQuery(id+"F0.wireOp",EDGE,"E0.top")])]});
            var sketch = newSketch(context, id + "F34", { "sketchPlane" : qUnion([Q0])});
            skLineSegment(sketch, "E110", {"start": v(10.75, 50) * mm, "end": v(-12.25, 50) * mm});
            skPoint(sketch, "E111", {"position": v(-12.25, 50) * mm});
            skLineSegment(sketch, "E112", {"start": v(-12.25, 50) * mm, "end": v(-12.25, 0) * mm});
            skPoint(sketch, "E113", {"position": v(-12.25, 0) * mm});
            skSolve(sketch);
        }
    });
